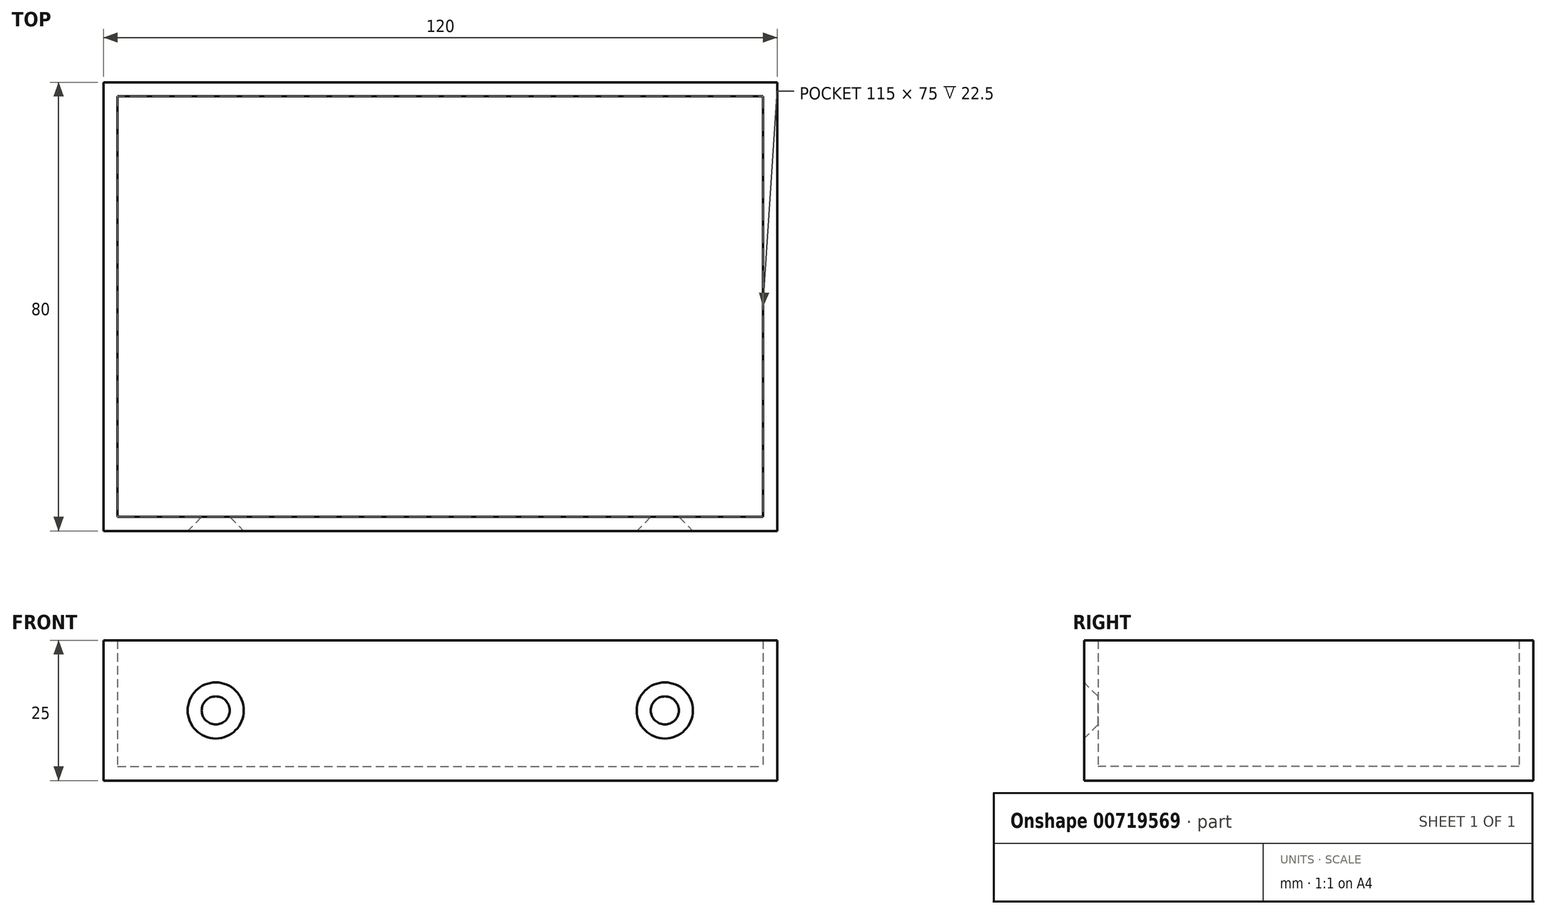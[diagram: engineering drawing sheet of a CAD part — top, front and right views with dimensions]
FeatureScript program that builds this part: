
annotation { "Feature Type Name" : "Feature", "Feature Type Description" : "" }
export const myFeature = defineFeature(function(context is Context, id is Id, definition is map)
    precondition{}
    {
        {
            var Q0;
            Q0=qCreatedBy(makeId("Top.planeOp"),FACE);
            var sketch = newSketch(context, id + "F0", { "sketchPlane" : qUnion([Q0])});
            skLineSegment(sketch, "E0.bottom", {"start": v(-55, 38.33) * mm, "end": v(65, 38.33) * mm});
            skLineSegment(sketch, "E0.top", {"start": v(-55, -41.67) * mm, "end": v(65, -41.67) * mm});
            skLineSegment(sketch, "E0.left", {"start": v(-55, 38.33) * mm, "end": v(-55, -41.67) * mm});
            skLineSegment(sketch, "E0.right", {"start": v(65, 38.33) * mm, "end": v(65, -41.67) * mm});
            skSolve(sketch);
        }
        {
            var Q0;
            Q0=makeQuery(id+"F0.imprint","IMPRINT",FACE,{"disambiguationData":[TD([[makeQuery(id+"F0.imprint","IMPRINT",EDGE,{"derivedFrom":sQuery(id+"F0.wireOp",EDGE,"E0.bottom")}),-1.0]])]});
            extrude(context, id + "F1", {"entities" : qUnion([Q0]), "depth" : 25 * mm, "offsetDistance" : 25 * mm});
        }
        {
            var Q0;
            Q0=makeQuery(id+"F1.opExtrude","CAP_FACE",FACE,{"disambiguationData":[OSD([sQuery(id+"F0.wireOp",EDGE,"E0.bottom"),sQuery(id+"F0.wireOp",EDGE,"E0.top"),sQuery(id+"F0.wireOp",EDGE,"E0.left"),sQuery(id+"F0.wireOp",EDGE,"E0.right")])],"isStart":false});
            shell(context, id + "F2", {"entities" : qUnion([Q0]), "thickness" : 2.5 * mm});
        }
        {
            var Q0;
            Q0=makeQuery(id+"F1.opExtrude","SWEPT_FACE",FACE,{"disambiguationData":[OSD([sQuery(id+"F0.wireOp",EDGE,"E0.top")])]});
            var sketch = newSketch(context, id + "F3", { "sketchPlane" : qUnion([Q0])});
            skCircle(sketch, "E1", {"center": v(-35, 12.5) * mm, "radius": 2.5 * mm});
            skPoint(sketch, "E1.centerSnap0", {"position": v(-55, 12.5) * mm});
            skCircle(sketch, "E2", {"center": v(45, 12.5) * mm, "radius": 7.4 * mm});
            skPoint(sketch, "E2.centerSnap0", {"position": v(65, 12.5) * mm});
            skSolve(sketch);
        }
        {
            var Q0;
            Q0=sQuery(id+"F3.wireOp",VERTEX,"E1.center");
            var Q1;
            Q1=makeQuery(id+"F1.opExtrude","SWEPT_BODY",BODY,{"disambiguationData":[OSD([sQuery(id+"F0.wireOp",EDGE,"E0.bottom"),sQuery(id+"F0.wireOp",EDGE,"E0.top"),sQuery(id+"F0.wireOp",EDGE,"E0.left"),sQuery(id+"F0.wireOp",EDGE,"E0.right")])]});
            hole(context, id + "F4", {"style" : HoleStyle.C_SINK, "endStyle" : HoleEndStyle.BLIND, "holeDiameter" : 5 * mm, "cSinkDiameter" : 10 * mm, "cSinkAngle" : 90 * degree, "majorDiameter" : 5 * mm, "holeDepth" : 12 * mm, "isTappedThrough" : true, "tappedDepth" : 12 * mm, "tapClearance" : 3, "startFromSketch" : true, "locations" : qUnion([Q0]), "scope" : qUnion([Q1])});
        }
        {
            var Q0;
            Q0=sQuery(id+"F3.wireOp",VERTEX,"E2.center");
            var Q1;
            Q1=makeQuery(id+"F1.opExtrude","SWEPT_BODY",BODY,{"disambiguationData":[OSD([sQuery(id+"F0.wireOp",EDGE,"E0.bottom"),sQuery(id+"F0.wireOp",EDGE,"E0.top"),sQuery(id+"F0.wireOp",EDGE,"E0.left"),sQuery(id+"F0.wireOp",EDGE,"E0.right")])]});
            hole(context, id + "F5", {"style" : HoleStyle.C_SINK, "endStyle" : HoleEndStyle.BLIND, "holeDiameter" : 5 * mm, "cSinkDiameter" : 10 * mm, "cSinkAngle" : 90 * degree, "majorDiameter" : 5 * mm, "holeDepth" : 12 * mm, "isTappedThrough" : true, "tappedDepth" : 12 * mm, "tapClearance" : 3, "startFromSketch" : true, "locations" : qUnion([Q0]), "scope" : qUnion([Q1])});
        }
    });
